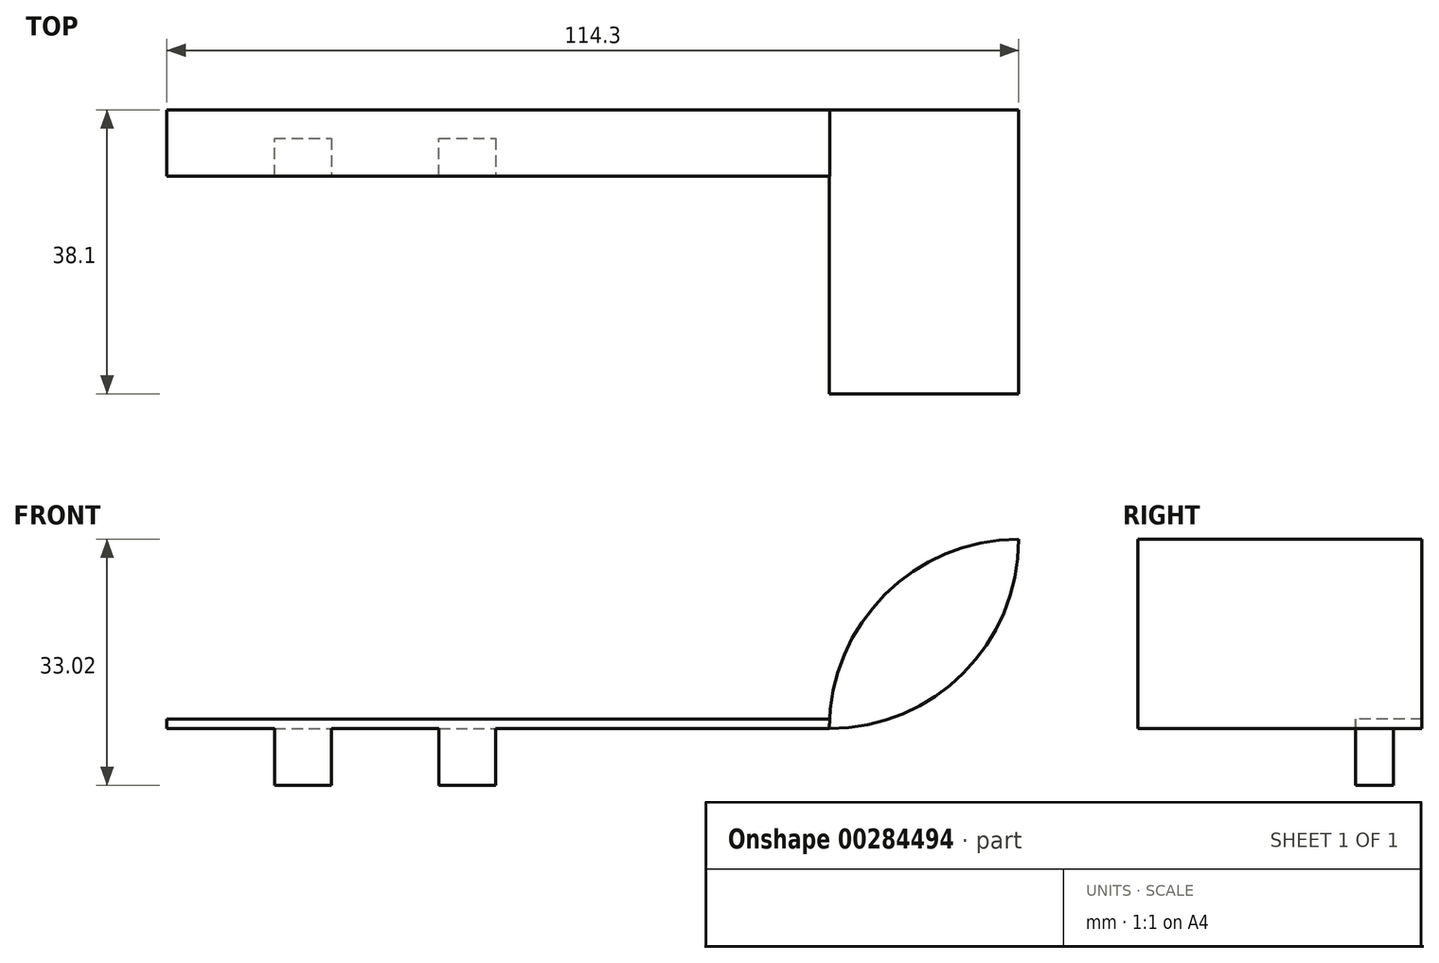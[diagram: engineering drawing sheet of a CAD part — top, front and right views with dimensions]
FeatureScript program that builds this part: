
annotation { "Feature Type Name" : "Feature", "Feature Type Description" : "" }
export const myFeature = defineFeature(function(context is Context, id is Id, definition is map)
    precondition{}
    {
        {
            var Q0;
            Q0=qCreatedBy(makeId("Top.planeOp"),FACE);
            var sketch = newSketch(context, id + "F0", { "sketchPlane" : qUnion([Q0])});
            skLineSegment(sketch, "E0.bottom", {"start": v(-145.43, 32.32) * mm, "end": v(-56.53, 32.32) * mm});
            skLineSegment(sketch, "E0.top", {"start": v(-145.43, 23.43) * mm, "end": v(-56.53, 23.43) * mm});
            skLineSegment(sketch, "E0.left", {"start": v(-145.43, 32.32) * mm, "end": v(-145.43, 23.43) * mm});
            skLineSegment(sketch, "E0.right", {"start": v(-56.53, 32.32) * mm, "end": v(-56.53, 23.43) * mm});
            skLineSegment(sketch, "E1", {"start": v(-86.78, 37.64) * mm, "end": v(-86.78, 0) * mm, "construction": true});
            skLineSegment(sketch, "E2", {"start": v(-130.98, 23.43) * mm, "end": v(-130.98, 28.5) * mm});
            skLineSegment(sketch, "E3", {"start": v(-130.98, 28.5) * mm, "end": v(-123.36, 28.5) * mm});
            skLineSegment(sketch, "E4", {"start": v(-123.36, 28.5) * mm, "end": v(-123.36, 23.43) * mm});
            skLineSegment(sketch, "E5", {"start": v(-108.9, 23.43) * mm, "end": v(-108.9, 28.5) * mm});
            skLineSegment(sketch, "E6", {"start": v(-108.9, 28.5) * mm, "end": v(-101.29, 28.5) * mm});
            skLineSegment(sketch, "E7", {"start": v(-101.29, 28.5) * mm, "end": v(-101.29, 23.43) * mm});
            skLineSegment(sketch, "E8", {"start": v(-56.53, 32.32) * mm, "end": v(-31.13, 32.32) * mm});
            skLineSegment(sketch, "E9", {"start": v(-31.13, 32.32) * mm, "end": v(-31.13, -5.78) * mm});
            skLineSegment(sketch, "E10", {"start": v(-31.13, -5.78) * mm, "end": v(-56.53, -5.78) * mm});
            skLineSegment(sketch, "E11", {"start": v(-56.53, -5.78) * mm, "end": v(-56.53, 23.43) * mm});
            skSolve(sketch);
        }
        {
            var Q0;
            Q0=makeQuery(id+"F0.imprint","IMPRINT",FACE,{"disambiguationData":[TD([[makeQuery(id+"F0.imprint","IMPRINT",EDGE,{"derivedFrom":sQuery(id+"F0.wireOp",EDGE,"E0.bottom")}),-1.0]])]});
            extrude(context, id + "F1", {"entities" : qUnion([Q0]), "depth" : 1.27 * mm});
        }
        {
            var Q0;
            {var subQ0=sQuery(id+"F0.wireOp",EDGE,"E2");Q0=makeQuery(id+"F0.imprint","IMPRINT",FACE,{"disambiguationData":[TD([[makeQuery(id+"F0.imprint","IMPRINT",EDGE,{"derivedFrom":subQ0}),-1.0]])]});}
            var Q1;
            {var subQ0=sQuery(id+"F0.wireOp",EDGE,"E5");Q1=makeQuery(id+"F0.imprint","IMPRINT",FACE,{"disambiguationData":[TD([[makeQuery(id+"F0.imprint","IMPRINT",EDGE,{"derivedFrom":subQ0}),-1.0]])]});}
            extrude(context, id + "F2", {"entities" : qUnion([Q0, Q1]), "oppositeDirection" : true, "depth" : 7.62 * mm});
        }
        {
            var Q0;
            {var subQ0=sQuery(id+"F0.wireOp",EDGE,"E2");Q0=makeQuery(id+"F0.imprint","IMPRINT",FACE,{"disambiguationData":[TD([[makeQuery(id+"F0.imprint","IMPRINT",EDGE,{"derivedFrom":subQ0}),-1.0]])]});}
            var Q1;
            {var subQ0=sQuery(id+"F0.wireOp",EDGE,"E5");Q1=makeQuery(id+"F0.imprint","IMPRINT",FACE,{"disambiguationData":[TD([[makeQuery(id+"F0.imprint","IMPRINT",EDGE,{"derivedFrom":subQ0}),-1.0]])]});}
            extrude(context, id + "F3", {"entities" : qUnion([Q0, Q1]), "operationType" : NewBodyOperationType.ADD, "depth" : 1.27 * mm});
        }
        {
            var Q0;
            Q0=makeQuery(id+"F0.imprint","IMPRINT",FACE,{"disambiguationData":[TD([[makeQuery(id+"F0.imprint","IMPRINT",EDGE,{"derivedFrom":sQuery(id+"F0.wireOp",EDGE,"E0.right")}),1.0]])]});
            extrude(context, id + "F4", {"entities" : qUnion([Q0]), "operationType" : NewBodyOperationType.ADD, "depth" : 25.4 * mm});
        }
        {
            var Q0;
            Q0=makeQuery(id+"F4.opExtrude","CAP_EDGE",EDGE,{"disambiguationData":[OSD([sQuery(id+"F0.wireOp",EDGE,"E9")])],"isStart":true});
            fillet(context, id + "F5", {"entities" : qUnion([Q0]), "radius" : 25.4 * mm, "tangentPropagation" : true, "allowEdgeOverflow" : false});
        }
        {
            var Q0;
            Q0=makeQuery(id+"F4.opExtrude","CAP_EDGE",EDGE,{"disambiguationData":[OSD([sQuery(id+"F0.wireOp",EDGE,"E0.right"),sQuery(id+"F0.wireOp",EDGE,"E11")])],"isStart":false});
            fillet(context, id + "F6", {"entities" : qUnion([Q0]), "radius" : 25.4 * mm, "tangentPropagation" : true, "allowEdgeOverflow" : false});
        }
    });
